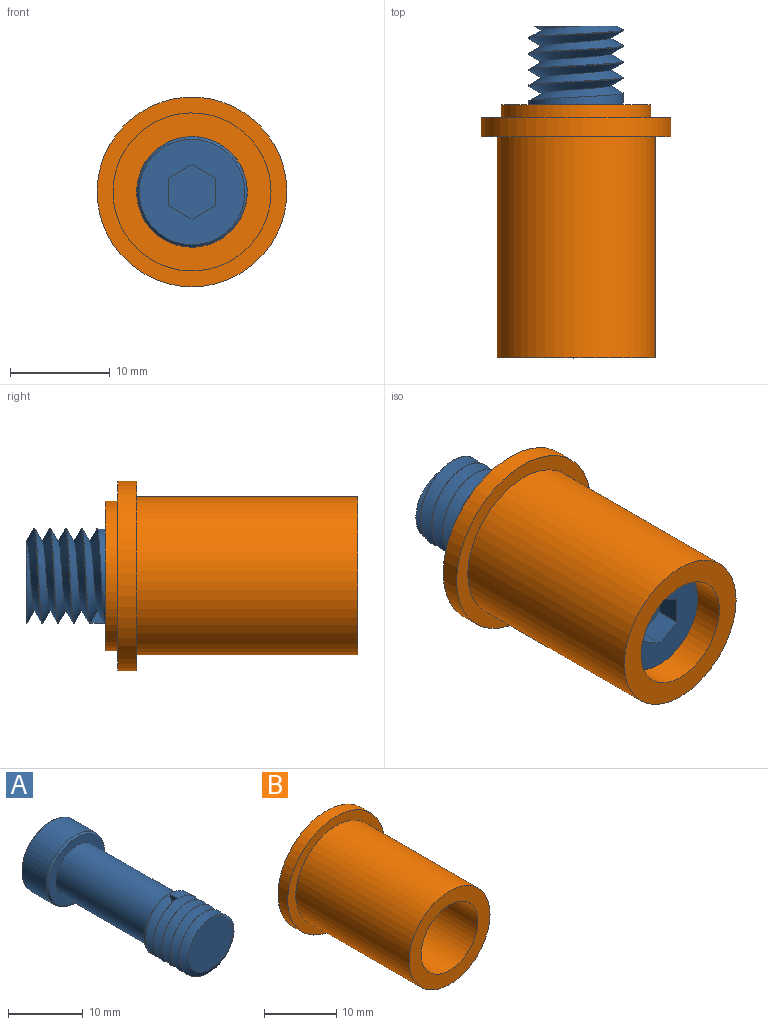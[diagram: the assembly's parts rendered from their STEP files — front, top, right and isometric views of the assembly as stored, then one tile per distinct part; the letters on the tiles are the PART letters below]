
ASSEMBLY  parts=2 mates=1
PART A: 19 faces, bbox 12.2x32.5x12.2 mm
  f0: cylinder r=4.76mm len=9.53mm, axis (0,1,0), area 31.8mm2, adj f5,f6,f16,f17,f18
  f1: plane 10.6x10.6mm, normal (0,1,0), area 68.7mm2, adj f7,f8,f9,f10,f11,f12,f15
  f2: cylinder r=3.97mm len=17.46mm, axis (0,1,0), area 435.5mm2, adj f4,f6
  f3: cylinder r=5.56mm len=11.11mm, axis (0,-1,0), area 159.6mm2, adj f14,f15
  f4: plane 10.6x10.6mm, normal (0,-1,0), area 38.8mm2, adj f2,f14
  f5: plane 9.38x9.35mm, normal (0,-1,0), area 54mm2, adj f0,f17,f18
  f6: plane 9.53x9.53mm, normal (0,1,0), area 21.8mm2, adj f0,f2
  f7: plane 2.75x2.54mm, normal (-1,0,0), area 7mm2, adj f1,f8,f12,f13
  f8: plane 2.54x2.38mm, normal (-0.5,0,0.87), area 7mm2, adj f1,f7,f9,f13
  f9: plane 2.54x2.38mm, normal (0.5,0,0.87), area 7mm2, adj f1,f8,f10,f13
  f10: plane 2.75x2.54mm, normal (1,0,0), area 7mm2, adj f1,f9,f11,f13
  f11: plane 2.54x2.38mm, normal (0.5,0,-0.87), area 7mm2, adj f1,f10,f12,f13
  f12: plane 2.54x2.38mm, normal (-0.5,0,-0.87), area 7mm2, adj f1,f7,f11,f13
  f13: plane 5.5x4.76mm, normal (0,1,0), area 19.6mm2, adj f7,f8,f9,f10,f11,f12
  f14: cone r=5.3mm half-angle=45deg, axis (0,1,0), area 12.3mm2, adj f3,f4
  f15: cone r=5.56mm half-angle=45deg, axis (0,-1,0), area 12.3mm2, adj f1,f3
  f16: plane 1.52x1.32mm, normal (-1,0,0), area 1mm2, adj f0,f17,f18
  f17: bspline ~11x9.53mm, area 187.7mm2, adj f0,f5,f16,f18
  f18: bspline ~11x9.53mm, area 168mm2, adj f0,f5,f16,f17
PART B: 12 faces, bbox 19.1x25.4x19.1 mm
  f0: plane 15.88x15.88mm, normal (0,-1,0), area 100.9mm2, adj f1,f3
  f1: cylinder r=5.56mm len=11.11mm, axis (0,-1,0), area 277.1mm2, adj f0,f2
  f2: plane 11.11x11.11mm, normal (0,-1,0), area 47.5mm2, adj f1,f11
  f3: cylinder r=7.94mm len=22.23mm, axis (0,-1,0), area 1108.4mm2, adj f0,f4
  f4: plane 19.05x19.05mm, normal (0,-1,0), area 87.1mm2, adj f3,f5
  f5: cylinder r=9.53mm len=19.05mm, axis (0,1,0), area 114mm2, adj f4,f7
  f6: cylinder r=7.51mm len=15.01mm, axis (0,1,0), area 59.9mm2, adj f7,f8
  f7: plane 19.05x19.05mm, normal (0,1,0), area 108mm2, adj f5,f6
  f8: plane 15.01x15.01mm, normal (0,1,0), area 105.7mm2, adj f6,f9
  f9: cylinder r=4.76mm len=9.53mm, axis (0,1,0), area 237.5mm2, adj f8,f10
  f10: plane 9.53x9.53mm, normal (0,1,0), area 21.8mm2, adj f9,f11
  f11: cylinder r=3.97mm len=9.53mm, axis (0,-1,0), area 237.5mm2, adj f2,f10
PLACE A rot(axis=(1,0,0),180deg) t=(1.31,-17.2,-3.11)mm
PLACE B t=(1.31,0.27,-3.11)mm
MATE cylindrical A.f2 <-> B.f1  axis (0,1,0) through (1.31,-17.2,-3.11)mm
